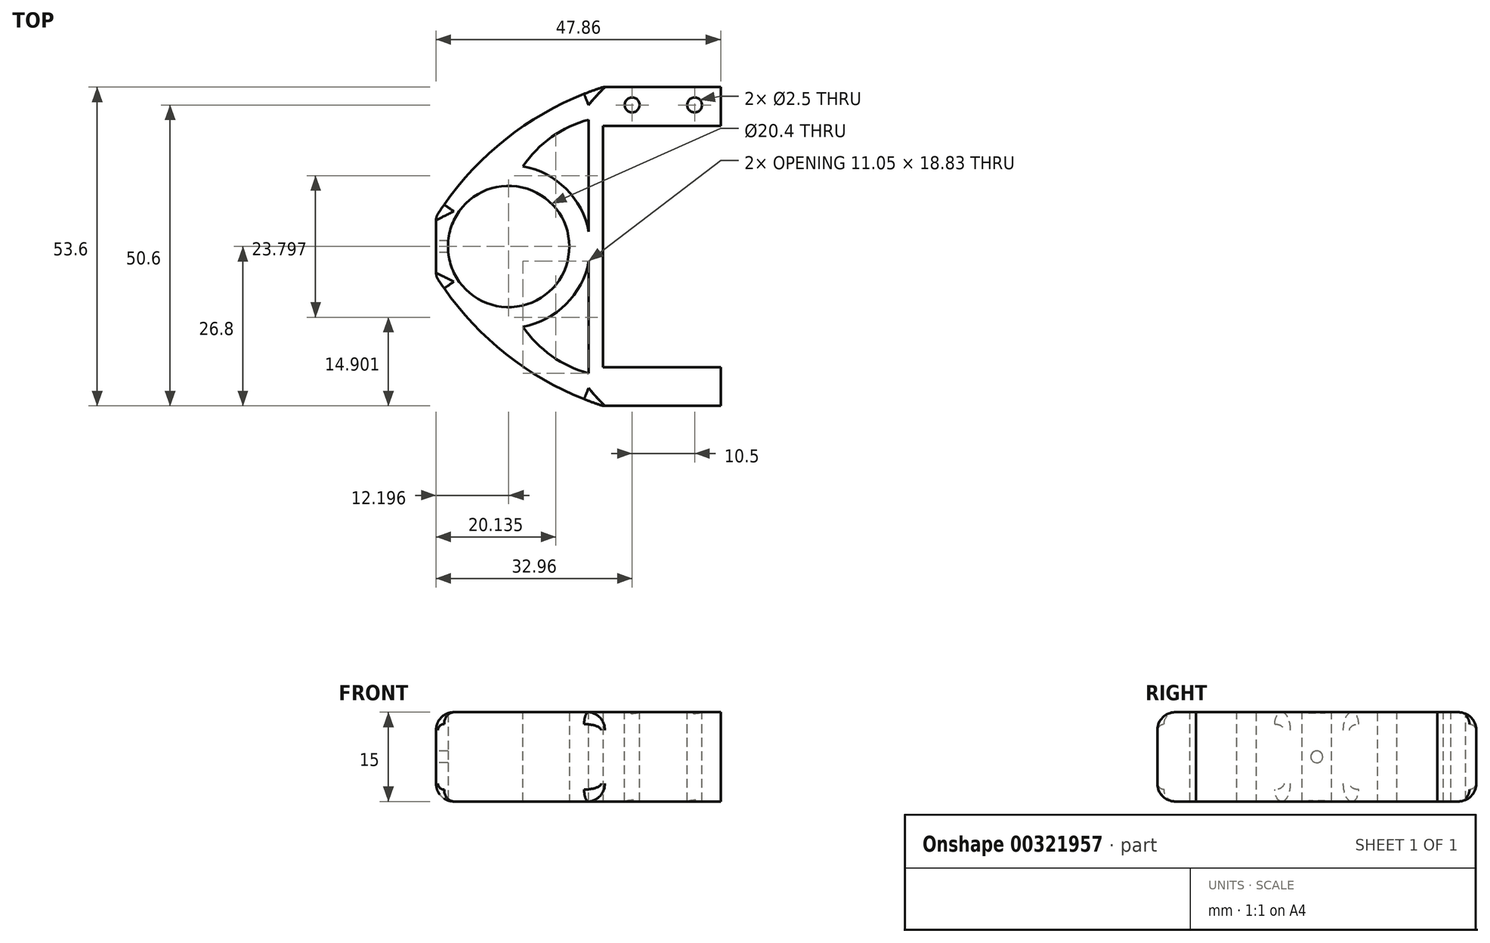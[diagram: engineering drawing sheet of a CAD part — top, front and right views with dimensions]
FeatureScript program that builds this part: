
annotation { "Feature Type Name" : "Feature", "Feature Type Description" : "" }
export const myFeature = defineFeature(function(context is Context, id is Id, definition is map)
    precondition{}
    {
        {
            var Q0;
            Q0=qCreatedBy(makeId("Top.planeOp"),FACE);
            var sketch = newSketch(context, id + "F0", { "sketchPlane" : qUnion([Q0])});
            skLineSegment(sketch, "E0.bottom", {"start": v(-14.61, 26.8) * mm, "end": v(15.25, 26.8) * mm});
            skLineSegment(sketch, "E0.top", {"start": v(-14.61, -26.8) * mm, "end": v(13.45, -26.8) * mm});
            skLineSegment(sketch, "E0.left", {"start": v(-14.61, 26.8) * mm, "end": v(-14.61, -26.8) * mm});
            skLineSegment(sketch, "E1", {"start": v(0, 43.02) * mm, "end": v(0, -42.03) * mm, "construction": true});
            skLineSegment(sketch, "E2", {"start": v(-70.85, 0) * mm, "end": v(82.27, 0) * mm, "construction": true});
            skCircle(sketch, "E3", {"center": v(-2.41, 0) * mm, "radius": 10.2 * mm});
            skLineSegment(sketch, "E4.bottom", {"start": v(13.45, -26.8) * mm, "end": v(33.25, -26.8) * mm});
            skLineSegment(sketch, "E4.top", {"start": v(13.45, -20.3) * mm, "end": v(33.25, -20.3) * mm});
            skLineSegment(sketch, "E4.right", {"start": v(33.25, -26.8) * mm, "end": v(33.25, -20.3) * mm});
            skLineSegment(sketch, "E5.MirrorCS", {"start": v(13.45, 20.3) * mm, "end": v(33.25, 20.3) * mm});
            skLineSegment(sketch, "E6.MirrorCS", {"start": v(33.25, 26.8) * mm, "end": v(33.25, 20.3) * mm});
            skLineSegment(sketch, "E7.MirrorCS", {"start": v(13.45, 26.8) * mm, "end": v(33.25, 26.8) * mm});
            skLineSegment(sketch, "E8.MirrorCS", {"start": v(13.45, 26.8) * mm, "end": v(13.45, 20.3) * mm});
            skLineSegment(sketch, "E9", {"start": v(13.45, -26.8) * mm, "end": v(13.45, -20.3) * mm});
            skLineSegment(sketch, "E10", {"start": v(13.45, -20.3) * mm, "end": v(13.45, 20.3) * mm});
            skArc(sketch, "E11", {"start": v(13.45, 26.8) * mm, "mid": v(-2.5, 18.36) * mm, "end": v(-14.61, 5) * mm});
            skArc(sketch, "E12.MirrorCS", {"start": v(13.45, -26.8) * mm, "mid": v(-2.5, -18.36) * mm, "end": v(-14.61, -5) * mm});
            skSolve(sketch);
        }
        {
            var Q0;
            Q0=makeQuery(id+"F0.imprint","IMPRINT",FACE,{"disambiguationData":[TD([[makeQuery(id+"F0.imprint","IMPRINT",EDGE,{"derivedFrom":sQuery(id+"F0.wireOp",EDGE,"E3")}),-1.0]])]});
            var Q1;
            Q1=makeQuery(id+"F0.imprint","IMPRINT",FACE,{"disambiguationData":[TD([[makeQuery(id+"F0.imprint","IMPRINT",EDGE,{"derivedFrom":sQuery(id+"F0.wireOp",EDGE,"E5.MirrorCS")}),1.0]])]});
            var Q2;
            Q2=makeQuery(id+"F0.imprint","IMPRINT",FACE,{"disambiguationData":[TD([[makeQuery(id+"F0.imprint","IMPRINT",EDGE,{"derivedFrom":sQuery(id+"F0.wireOp",EDGE,"E4.bottom")}),1.0]])]});
            extrude(context, id + "F1", {"entities" : qUnion([Q0, Q1, Q2]), "endBound" : BoundingType.SYMMETRIC, "depth" : 15 * mm});
        }
        {
            var Q0;
            Q0=makeQuery(id+"F1.opExtrude","SWEPT_FACE",FACE,{"disambiguationData":[OSD([sQuery(id+"F0.wireOp",EDGE,"E0.left")])]});
            var sketch = newSketch(context, id + "F2", { "sketchPlane" : qUnion([Q0])});
            skCircle(sketch, "E13", {"center": v(0, 0) * mm, "radius": 1 * mm});
            skSolve(sketch);
        }
        {
            var Q0;
            Q0 = qSketchRegion(id + "F2", true);
            extrude(context, id + "F3", {"entities" : qUnion([Q0]), "operationType" : NewBodyOperationType.REMOVE, "oppositeDirection" : true, "depth" : 5 * mm});
        }
        {
            var Q0;
            Q0=makeQuery(id+"F1.opExtrude","CAP_FACE",FACE,{"disambiguationData":[OSD([sQuery(id+"F0.wireOp",EDGE,"E0.bottom"),sQuery(id+"F0.wireOp",EDGE,"E0.top"),sQuery(id+"F0.wireOp",EDGE,"E0.left"),sQuery(id+"F0.wireOp",EDGE,"E3"),sQuery(id+"F0.wireOp",EDGE,"E4.bottom"),sQuery(id+"F0.wireOp",EDGE,"E4.top"),sQuery(id+"F0.wireOp",EDGE,"E4.right"),sQuery(id+"F0.wireOp",EDGE,"E5.MirrorCS"),sQuery(id+"F0.wireOp",EDGE,"E6.MirrorCS"),sQuery(id+"F0.wireOp",EDGE,"E7.MirrorCS"),sQuery(id+"F0.wireOp",EDGE,"E10")])],"isStart":false});
            var sketch = newSketch(context, id + "F4", { "sketchPlane" : qUnion([Q0])});
            skCircle(sketch, "E14", {"center": v(18.35, 23.8) * mm, "radius": 1.25 * mm});
            skLineSegment(sketch, "E15", {"start": v(13.45, 20.3) * mm, "end": v(13.45, 26.8) * mm, "construction": true});
            skCircle(sketch, "E16.MirrorC", {"center": v(28.85, 23.8) * mm, "radius": 1.25 * mm});
            skSolve(sketch);
        }
        {
            var Q0;
            Q0 = qSketchRegion(id + "F4", true);
            extrude(context, id + "F5", {"entities" : qUnion([Q0]), "operationType" : NewBodyOperationType.REMOVE, "endBound" : BoundingType.THROUGH_ALL, "oppositeDirection" : true, "depth" : 25 * mm});
        }
        {
            var Q0;
            Q0=makeQuery(id+"F1.opExtrude","CAP_EDGE",EDGE,{"disambiguationData":[OSD([sQuery(id+"F0.wireOp",EDGE,"E0.top"),sQuery(id+"F0.wireOp",EDGE,"E4.bottom")])],"isStart":false});
            var Q1;
            Q1=makeQuery(id+"F1.opExtrude","CAP_EDGE",EDGE,{"disambiguationData":[OSD([sQuery(id+"F0.wireOp",EDGE,"E0.left")])],"isStart":false});
            var Q2;
            Q2=makeQuery(id+"F1.opExtrude","CAP_EDGE",EDGE,{"disambiguationData":[OSD([sQuery(id+"F0.wireOp",EDGE,"E0.bottom"),sQuery(id+"F0.wireOp",EDGE,"E7.MirrorCS")])],"isStart":false});
            var Q3;
            Q3=makeQuery(id+"F1.opExtrude","CAP_EDGE",EDGE,{"disambiguationData":[OSD([sQuery(id+"F0.wireOp",EDGE,"E0.top"),sQuery(id+"F0.wireOp",EDGE,"E4.bottom")])],"isStart":true});
            var Q4;
            Q4=makeQuery(id+"F1.opExtrude","CAP_EDGE",EDGE,{"disambiguationData":[OSD([sQuery(id+"F0.wireOp",EDGE,"E0.left")])],"isStart":true});
            var Q5;
            Q5=makeQuery(id+"F1.opExtrude","CAP_EDGE",EDGE,{"disambiguationData":[OSD([sQuery(id+"F0.wireOp",EDGE,"E0.bottom"),sQuery(id+"F0.wireOp",EDGE,"E7.MirrorCS")])],"isStart":true});
            fillet(context, id + "F6", {"entities" : qUnion([Q0, Q1, Q2, Q3, Q4, Q5]), "radius" : 3 * mm, "tangentPropagation" : true, "allowEdgeOverflow" : false});
        }
        {
            var Q0;
            Q0=makeQuery(id+"F1.opExtrude","CAP_EDGE",EDGE,{"disambiguationData":[OSD([sQuery(id+"F0.wireOp",EDGE,"E12.MirrorCS")])],"isStart":false});
            var Q1;
            Q1=makeQuery(id+"F1.opExtrude","CAP_EDGE",EDGE,{"disambiguationData":[OSD([sQuery(id+"F0.wireOp",EDGE,"E11")])],"isStart":false});
            fillet(context, id + "F7", {"entities" : qUnion([Q0, Q1]), "radius" : 2 * mm, "tangentPropagation" : true, "allowEdgeOverflow" : false});
        }
        {
            var Q0;
            Q0=makeQuery(id+"F1.opExtrude","CAP_FACE",FACE,{"disambiguationData":[OSD([sQuery(id+"F0.wireOp",EDGE,"E0.left"),sQuery(id+"F0.wireOp",EDGE,"E3"),sQuery(id+"F0.wireOp",EDGE,"E4.bottom"),sQuery(id+"F0.wireOp",EDGE,"E4.top"),sQuery(id+"F0.wireOp",EDGE,"E4.right"),sQuery(id+"F0.wireOp",EDGE,"E5.MirrorCS"),sQuery(id+"F0.wireOp",EDGE,"E6.MirrorCS"),sQuery(id+"F0.wireOp",EDGE,"E7.MirrorCS"),sQuery(id+"F0.wireOp",EDGE,"E10"),sQuery(id+"F0.wireOp",EDGE,"E11"),sQuery(id+"F0.wireOp",EDGE,"E12.MirrorCS")])],"isStart":false});
            var sketch = newSketch(context, id + "F8", { "sketchPlane" : qUnion([Q0])});
            skLineSegment(sketch, "E17", {"start": v(-16.4, 0) * mm, "end": v(24.02, 0) * mm, "construction": true});
            skLineSegment(sketch, "E18", {"start": v(11.05, 2.48) * mm, "end": v(11.05, 21.31) * mm});
            skArc(sketch, "E19", {"start": v(11.05, 21.31) * mm, "mid": v(4.8, 18.4) * mm, "end": v(0, 13.48) * mm});
            skArc(sketch, "E20", {"start": v(11.05, 2.48) * mm, "mid": v(7.24, 9.7) * mm, "end": v(0, 13.48) * mm});
            skArc(sketch, "E21.MirrorCS", {"start": v(11.05, -21.31) * mm, "mid": v(4.8, -18.4) * mm, "end": v(0, -13.48) * mm});
            skArc(sketch, "E22.MirrorCS", {"start": v(11.05, -2.48) * mm, "mid": v(7.24, -9.7) * mm, "end": v(0, -13.48) * mm});
            skLineSegment(sketch, "E23.MirrorCS", {"start": v(11.05, -2.48) * mm, "end": v(11.05, -21.31) * mm});
            skSolve(sketch);
        }
        {
            var Q0;
            Q0 = qSketchRegion(id + "F8", true);
            extrude(context, id + "F9", {"entities" : qUnion([Q0]), "operationType" : NewBodyOperationType.REMOVE, "endBound" : BoundingType.THROUGH_ALL, "oppositeDirection" : true, "depth" : 25 * mm});
        }
    });
